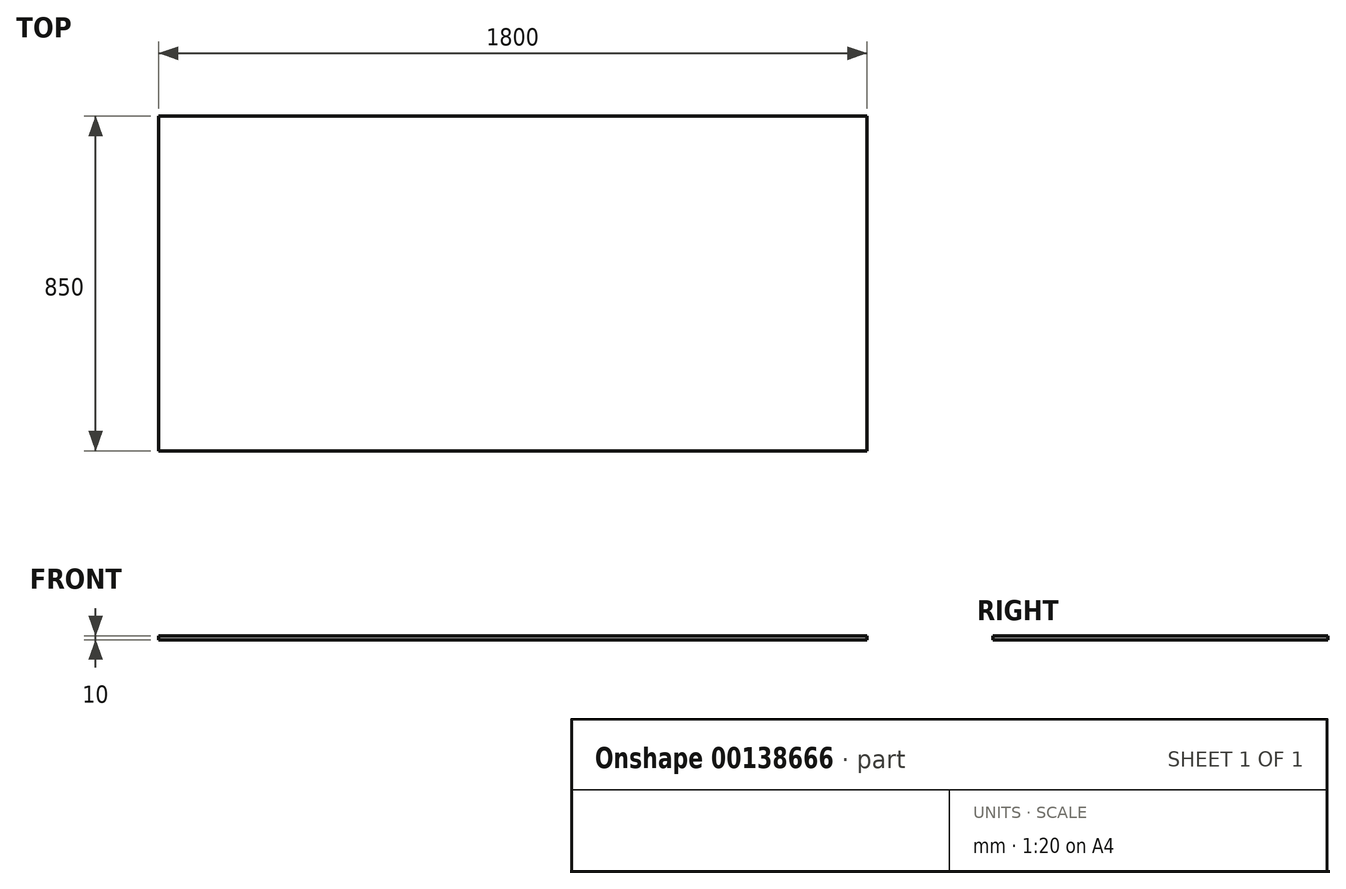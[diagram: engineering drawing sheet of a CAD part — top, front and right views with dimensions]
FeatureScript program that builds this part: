
annotation { "Feature Type Name" : "Feature", "Feature Type Description" : "" }
export const myFeature = defineFeature(function(context is Context, id is Id, definition is map)
    precondition{}
    {
        {
            var Q0;
            Q0=qCreatedBy(makeId("Top.planeOp"),FACE);
            var sketch = newSketch(context, id + "F0", { "sketchPlane" : qUnion([Q0])});
            skLineSegment(sketch, "E0.bottom", {"start": v(-1078.62, 530.8) * mm, "end": v(721.38, 530.8) * mm});
            skLineSegment(sketch, "E0.top", {"start": v(-1078.62, -319.2) * mm, "end": v(721.38, -319.2) * mm});
            skLineSegment(sketch, "E0.left", {"start": v(-1078.62, 530.8) * mm, "end": v(-1078.62, -319.2) * mm});
            skLineSegment(sketch, "E0.right", {"start": v(721.38, 530.8) * mm, "end": v(721.38, -319.2) * mm});
            skSolve(sketch);
        }
        {
            var Q0;
            Q0=makeQuery(id+"F0.imprint","IMPRINT",FACE,{"disambiguationData":[TD([[makeQuery(id+"F0.imprint","IMPRINT",EDGE,{"derivedFrom":sQuery(id+"F0.wireOp",EDGE,"E0.bottom")}),-1.0]])]});
            extrude(context, id + "F1", {"entities" : qUnion([Q0]), "depth" : 10 * mm});
        }
    });
